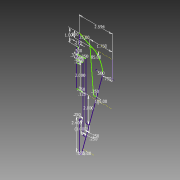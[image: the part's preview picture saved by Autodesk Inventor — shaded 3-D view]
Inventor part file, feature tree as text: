
AUTODESK INVENTOR PART (.ipt)
format: ipt  version: 2015 (Build 190159000, 159)  size: 101,376 bytes
history: native  units: in
note: dims shown in document units (in); Inventor stores cm internally (conversion verified against a paired STEP export)
features: sketch x1
ambient origin geometry x8: Origin, YZ Plane, XZ Plane, XY Plane, X Axis, Y Axis, Z Axis, Center Point
feature tree (1):
  sketch  "Sketch1"  dims[d8=3.0in d19=0.5841in d29=0.75in d35=1.0in d36=0.2185in d39=2.594in d43=0.5841in d44=0.5in d45=1.844in d46=0.5in d47=1.75in d48=0.25in d49=105.0deg d50=0.5in d51=0.5in d52=0.25in d54=0.375in d56=2.0in d59=0.5in d60=0.25in d61=0.234in d64=0.25in d67=2.0in d68=0.25in d69=105.0deg d70=0.125in d71=0.25in d75=2.3995in d76=0.125in d77=0.25in d78=1.0in d80=0.1374in d82=1.675in d83=0.1443in d84=1.6531in d86=0.1718in]
